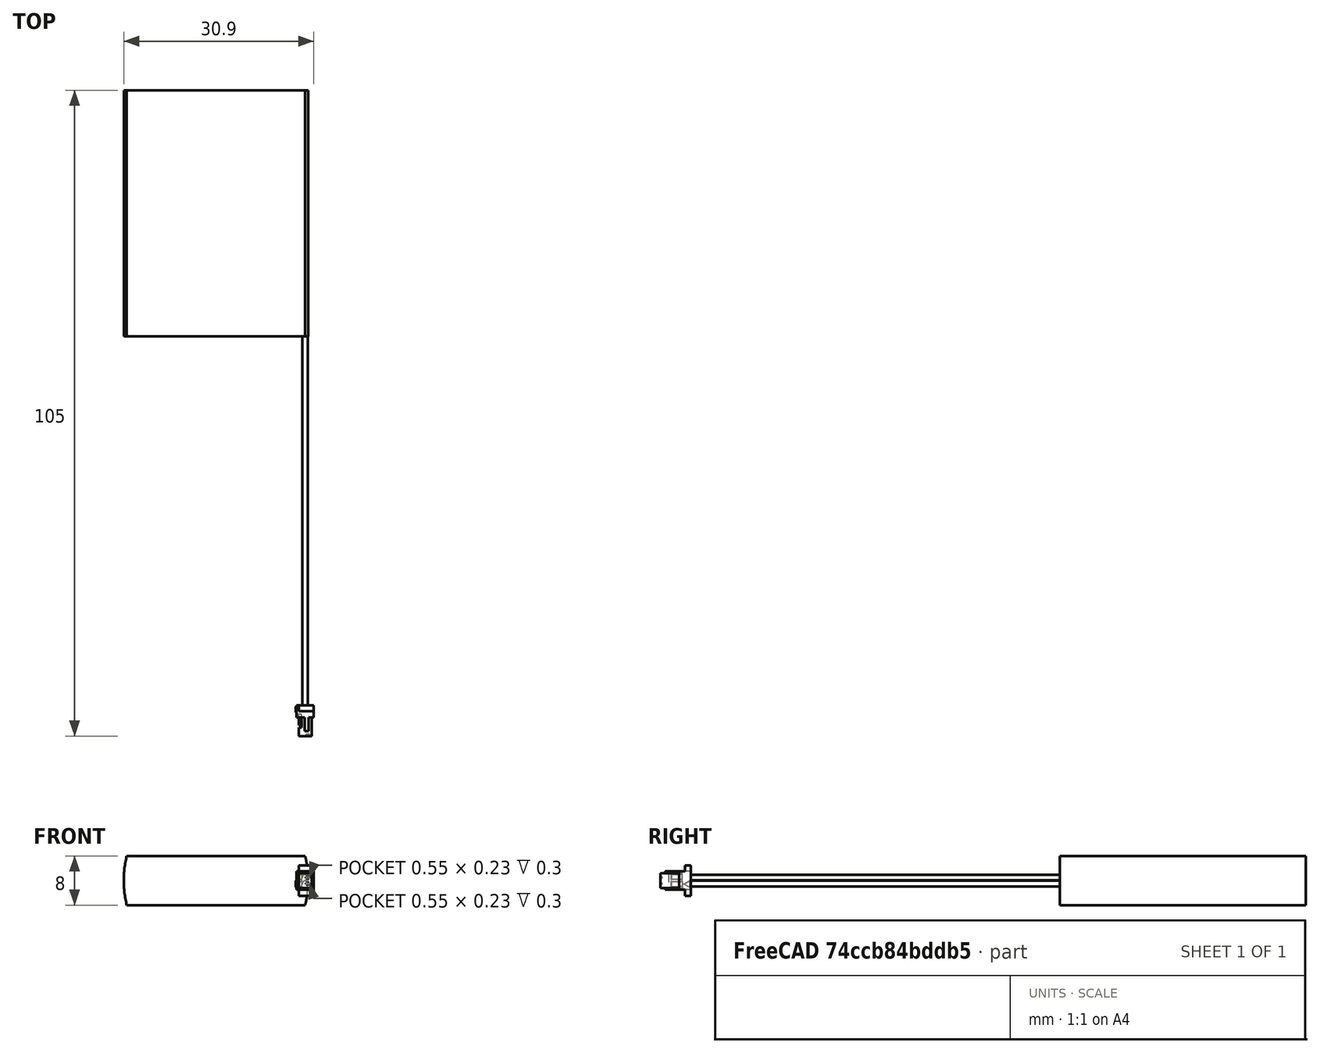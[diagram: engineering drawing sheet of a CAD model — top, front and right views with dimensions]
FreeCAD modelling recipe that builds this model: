
FCSTD DOCUMENT  (FreeCAD 2021.519R24301 +3652 (Git))
Label: ASR00012_1000mAh
License: Other
objects: TechDraw::DrawViewDimension×4, Sketcher::SketchObject×3, PartDesign::Pad×3, TechDraw::DrawViewPart×2, TechDraw::DrawViewAnnotation×2, PartDesign::Pocket×1, PartDesign::Mirrored×1, PartDesign::Body×1, Part::Feature×1, Part::MultiFuse×1, TechDraw::DrawSVGTemplate×1, TechDraw::DrawPage×1, Mesh::Feature×1
note: 21 computed .brp shape members not serialized (recipe doc carries the construction recipe); baked Part::Feature solids carry a one-line shape summary decoded from their .brp

FEATURE [Sketcher::SketchObject] Sketch
  FullyConstrained = true
  MapMode = 5
  Support = -> [XY_Plane]
  sketch-geometry (4):
    g0: LineSegment StartX=-15 StartY=20 StartZ=0 EndX=15 EndY=20 EndZ=0
    g1: LineSegment StartX=15 StartY=20 StartZ=0 EndX=15 EndY=-20 EndZ=0
    g2: LineSegment StartX=15 StartY=-20 StartZ=0 EndX=-15 EndY=-20 EndZ=0
    g3: LineSegment StartX=-15 StartY=-20 StartZ=0 EndX=-15 EndY=20 EndZ=0
  constraints (10):
    c: Coincident(g0,g1)
    c: Coincident(g1,g2)
    c: Coincident(g2,g3)
    c: Coincident(g3,g0)
    c: Horizontal(g2)
    c: Vertical(g1)
    c: Symmetric(g0,g2,g-1)
    c: Symmetric(g0,g0,g-2)
    c: DistanceX(g0,g0) = 30
    c: DistanceY(g3,g3) = 40
FEATURE [PartDesign::Pad] Pad
  ClaimChildren = false
  Direction = (1,1,1)
  Fit = 0
  FitJoin = 0
  InnerFit = 0
  InnerFitJoin = 0
  InnerTaperAngle = 0
  InnerTaperAngleRev = 0
  Length = 8
  Length2 = 100
  Midplane = true
  NewSolid = false
  Profile = -> Sketch
  Suppress = false
  Type = 0
FEATURE [Sketcher::SketchObject] Sketch001
  ExternalGeometry = -> [Pad]
  FullyConstrained = true
  MapMode = 5
  Placement = pos=(0,20,0) rot=(0,0.707107,0.707107;3.14159rad)
  Support = -> [Pad]
  sketch-geometry (5):
    g0: ArcOfCircle CenterX=1.25 CenterY=1.7e-15 CenterZ=0 NormalX=0 NormalY=0 NormalZ=1 AngleXU=0 Radius=16.25 StartAngle=2.89288 EndAngle=3.3903
    g1: LineSegment [constr] StartX=-14.5 StartY=-4 StartZ=0 EndX=-14.5 EndY=4 EndZ=0
    g2: LineSegment StartX=-14.5 StartY=-4 StartZ=0 EndX=-16 EndY=-4 EndZ=0
    g3: LineSegment StartX=-14.5 StartY=4 StartZ=0 EndX=-16 EndY=4 EndZ=0
    g4: LineSegment StartX=-16 StartY=4 StartZ=0 EndX=-16 EndY=-4 EndZ=0
  constraints (15):
    c: PointOnObject(g0,g-5)
    c: PointOnObject(g0,g-4)
    c: Tangent(g0,g-3)
    c: Coincident(g1,g0)
    c: Coincident(g1,g0)
    c: Vertical(g1)
    c: Coincident(g2,g0)
    c: Horizontal(g2)
    c: Coincident(g3,g0)
    c: Horizontal(g3)
    c: Coincident(g4,g3)
    c: Coincident(g4,g2)
    c: Vertical(g4)
    c: DistanceX(g3,g-4) = 1
    c: DistanceX(g-4,g0) = 0.5
FEATURE [PartDesign::Pocket] Pocket
  BaseFeature = -> Pad
  ClaimChildren = false
  Fit = 0
  FitJoin = 0
  InnerFit = 0
  InnerFitJoin = 0
  InnerTaperAngle = 0
  InnerTaperAngleRev = 0
  Length = 5
  Length2 = 100
  NewSolid = false
  Profile = -> Sketch001
  Suppress = false
  Type = 1
FEATURE [PartDesign::Mirrored] Mirrored
  BaseFeature = -> Pocket
  CopyShape = true
  MirrorPlane = -> Sketch001 [V_Axis]
  NewSolid = false
  OriginalSubs = -> [Pocket]
  Originals = -> [Pocket]
  ParallelTransform = true
  SubTransform = true
  Suppress = false
FEATURE [PartDesign::Pad] Pad001
  BaseFeature = -> Mirrored
  ClaimChildren = false
  Direction = (1,1,1)
  Fit = 0
  FitJoin = 0
  InnerFit = 0
  InnerFitJoin = 0
  InnerTaperAngle = 0
  InnerTaperAngleRev = 0
  Length = 7.85
  Length2 = 100
  NewSolid = false
  Profile = -> Mirrored [Face8]
  Reversed = true
  Suppress = false
  Type = 0
FEATURE [Sketcher::SketchObject] Sketch002
  ExternalGeometry = -> [Pad001]
  FullyConstrained = true
  MapMode = 5
  Placement = pos=(0,-20,0) rot=(1,0,0;1.5708rad)
  Support = -> [Pad001]
  sketch-geometry (7):
    g0: Circle CenterX=14.5 CenterY=-0.5 CenterZ=0 NormalX=0 NormalY=0 NormalZ=1 AngleXU=0 Radius=0.45
    g1: Circle CenterX=14.5 CenterY=0.5 CenterZ=0 NormalX=0 NormalY=0 NormalZ=1 AngleXU=0 Radius=0.45
    g2: LineSegment [constr] StartX=14.5 StartY=0.5 StartZ=0 EndX=14.5 EndY=-0.5 EndZ=0
    g3: GeomPoint [constr] X=14.5 Y=-0.95 Z=0
    g4: GeomPoint [constr] X=14.5 Y=0.95 Z=0
    g5: LineSegment [constr] StartX=14.05 StartY=-0.5 StartZ=0 EndX=14.95 EndY=-0.5 EndZ=0
    g6: GeomPoint [constr] X=14.5 Y=0.05 Z=0
  constraints (16):
    c: Coincident(g2,g1)
    c: Coincident(g2,g0)
    c: Equal(g0,g1)
    c: Diameter(g0) = 0.9
    c: Symmetric(g0,g1,g-1)
    c: PointOnObject(g3,g2)
    c: PointOnObject(g4,g1)
    c: Symmetric(g3,g4,g-1)
    c: PointOnObject(g5,g0)
    c: PointOnObject(g5,g0)
    c: Horizontal(g5)
    c: PointOnObject(g0,g5)
    c: PointOnObject(g6,g1)
    c: PointOnObject(g6,g2)
    c: DistanceX(g5,g-3) = 0.05
    c: DistanceY(g-3,g6) = 0.05
FEATURE [PartDesign::Pad] Pad002
  BaseFeature = -> Pad001
  ClaimChildren = false
  Direction = (1,1,1)
  Fit = 0
  FitJoin = 0
  InnerFit = 0
  InnerFitJoin = 0
  InnerTaperAngle = 0
  InnerTaperAngleRev = 0
  Length = 60
  Length2 = 100
  NewSolid = false
  Profile = -> Sketch002
  Suppress = false
  Type = 0
FEATURE [PartDesign::Body] Body
  AutoGroupSolids = false
  ExportMode = 0
  Group = -> [Sketch,Pad,Sketch001,Pocket,Mirrored,Pad001,Sketch002,Pad002]
  Origin = -> Origin
  Tip = -> Pad002
  _ExportChildren = -> [Pad,Pocket,Mirrored,Pad001,Pad002]
  _GroupVersion = 1
FEATURE [Part::Feature] Solid  label="Body007"
  Placement = pos=(13.2155,-82,1.39e-14) rot=(0,0,1;0rad)
  shape: bbox 2.9 x 5 x 4.94 mm, 60 faces (baked)
FEATURE [Part::MultiFuse] Fusion
  Shapes = -> [Body,Solid]
FEATURE [TechDraw::DrawSVGTemplate] Template
  Height = 210
  Orientation = 1
  Width = 297
FEATURE [TechDraw::DrawViewPart] View
  CoarseView = false
  Direction = (0,0,1)
  Focus = 100
  HardHidden = false
  IsoCount = 0
  IsoHidden = false
  IsoVisible = false
  LockPosition = false
  Perspective = false
  Rotation = 180
  Scale = 1.043
  ScaleType = 0
  SeamHidden = false
  SeamVisible = true
  SmoothHidden = false
  SmoothVisible = true
  Source = -> [Fusion]
  X = 178.5
  XDirection = (1,0,0)
  Y = 105
FEATURE [TechDraw::DrawViewPart] View001
  CoarseView = false
  Direction = (-1,0,0)
  Focus = 100
  HardHidden = false
  IsoCount = 0
  IsoHidden = false
  IsoVisible = false
  LockPosition = false
  Perspective = false
  Rotation = 90
  Scale = 1.043
  ScaleType = 0
  SeamHidden = false
  SeamVisible = true
  SmoothHidden = false
  SmoothVisible = true
  Source = -> [Fusion]
  X = 118.5
  XDirection = (0,-1,0)
  Y = 105
FEATURE [TechDraw::DrawViewAnnotation] Annotation
  Font = MS Shell Dlg 2
  LineSpace = 80
  LockPosition = false
  MaxWidth = -1
  Rotation = 0
  ScaleType = 0
  Text = SIDE VIEW
  TextSize = 6
  TextStyle = 0
  X = 118.5
  Y = 162
FEATURE [TechDraw::DrawViewAnnotation] Annotation001
  Font = MS Shell Dlg 2
  LineSpace = 80
  LockPosition = false
  MaxWidth = -1
  Rotation = 0
  ScaleType = 0
  Text = TOP VIEW
  TextSize = 6
  TextStyle = 0
  X = 178.5
  Y = 162
FEATURE [TechDraw::DrawViewDimension] Dimension
  Arbitrary = false
  ArbitraryTolerances = false
  EqualTolerance = true
  FormatSpec = %.1f
  FormatSpecOverTolerance = %+.1f
  FormatSpecUnderTolerance = %+.1f
  Inverted = false
  LockPosition = false
  MeasureType = 1
  OverTolerance = 0.5
  References2D = -> [View001]
  Rotation = 0
  ScaleType = 0
  TheoreticalExact = false
  Type = 1
  UnderTolerance = -0.5
  X = -32
  Y = -59
FEATURE [TechDraw::DrawViewDimension] Dimension001
  Arbitrary = false
  ArbitraryTolerances = false
  EqualTolerance = true
  FormatSpec = %.1f
  FormatSpecOverTolerance = %+.1f
  FormatSpecUnderTolerance = %+.1f
  Inverted = false
  LockPosition = false
  MeasureType = 1
  OverTolerance = 2
  References2D = -> [View]
  Rotation = 0
  ScaleType = 0
  TheoreticalExact = false
  Type = 1
  UnderTolerance = -2
  X = 33.4693
  Y = -59
FEATURE [TechDraw::DrawViewDimension] Dimension002
  Arbitrary = false
  ArbitraryTolerances = false
  EqualTolerance = true
  FormatSpec = %.1f
  FormatSpecOverTolerance = %+.1f
  FormatSpecUnderTolerance = %+.1f
  Inverted = false
  LockPosition = false
  MeasureType = 1
  OverTolerance = 3
  References2D = -> [View]
  Rotation = 0
  ScaleType = 0
  TheoreticalExact = false
  Type = 2
  UnderTolerance = -3
  X = -32
  Y = -32.8975
FEATURE [TechDraw::DrawViewDimension] Dimension003
  Arbitrary = false
  ArbitraryTolerances = false
  EqualTolerance = true
  FormatSpec = %.1f
  FormatSpecOverTolerance = %+.1f
  FormatSpecUnderTolerance = %+.1f
  Inverted = false
  LockPosition = false
  MeasureType = 1
  OverTolerance = 5
  References2D = -> [View]
  Rotation = 0
  ScaleType = 0
  TheoreticalExact = false
  Type = 2
  UnderTolerance = -5
  X = -32
  Y = 19.2525
FEATURE [TechDraw::DrawPage] Page
  KeepUpdated = true
  NextBalloonIndex = 1
  ProjectionType = 0
  Template = -> Template
  Views = -> [View,View001,Annotation,Annotation001,Dimension,Dimension001,Dimension002,Dimension003]
FEATURE [Mesh::Feature] Mesh  label="Fusion (Meshed)"
